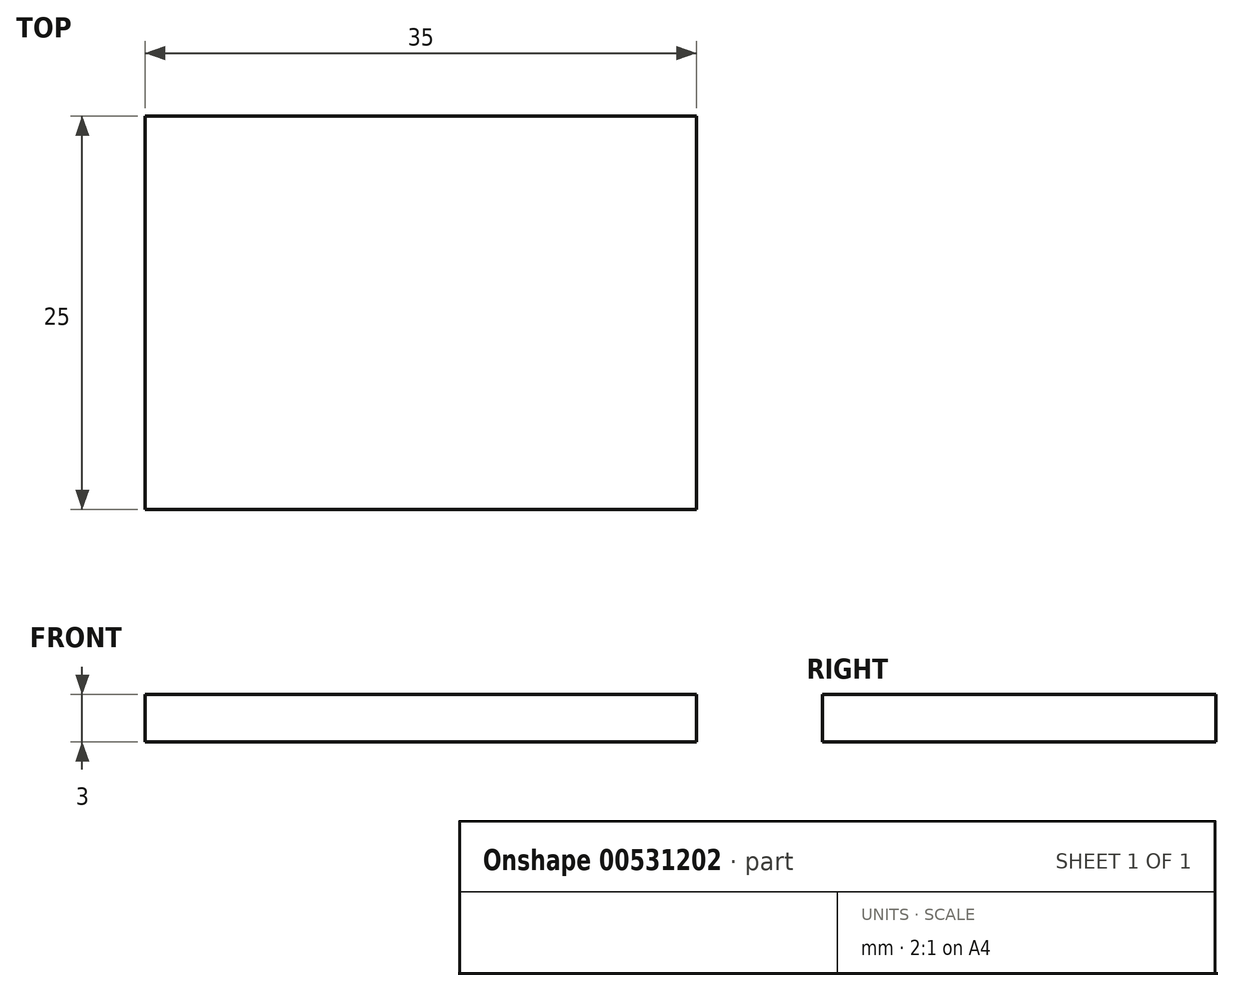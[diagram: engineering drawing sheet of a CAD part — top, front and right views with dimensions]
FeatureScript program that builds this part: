
annotation { "Feature Type Name" : "Feature", "Feature Type Description" : "" }
export const myFeature = defineFeature(function(context is Context, id is Id, definition is map)
    precondition{}
    {
        {
            var Q0;
            Q0=qCreatedBy(makeId("Top.planeOp"),FACE);
            var sketch = newSketch(context, id + "F0", { "sketchPlane" : qUnion([Q0])});
            skLineSegment(sketch, "E0.bottom", {"start": v(-111.56, 0) * mm, "end": v(-76.56, 0) * mm});
            skLineSegment(sketch, "E0.top", {"start": v(-111.56, -25) * mm, "end": v(-76.56, -25) * mm});
            skLineSegment(sketch, "E0.left", {"start": v(-111.56, 0) * mm, "end": v(-111.56, -25) * mm});
            skLineSegment(sketch, "E0.right", {"start": v(-76.56, 0) * mm, "end": v(-76.56, -25) * mm});
            skSolve(sketch);
        }
        {
            var Q0;
            Q0 = qSketchRegion(id + "F0", true);
            extrude(context, id + "F1", {"entities" : qUnion([Q0]), "depth" : 3 * mm, "offsetDistance" : 25 * mm});
        }
    });
